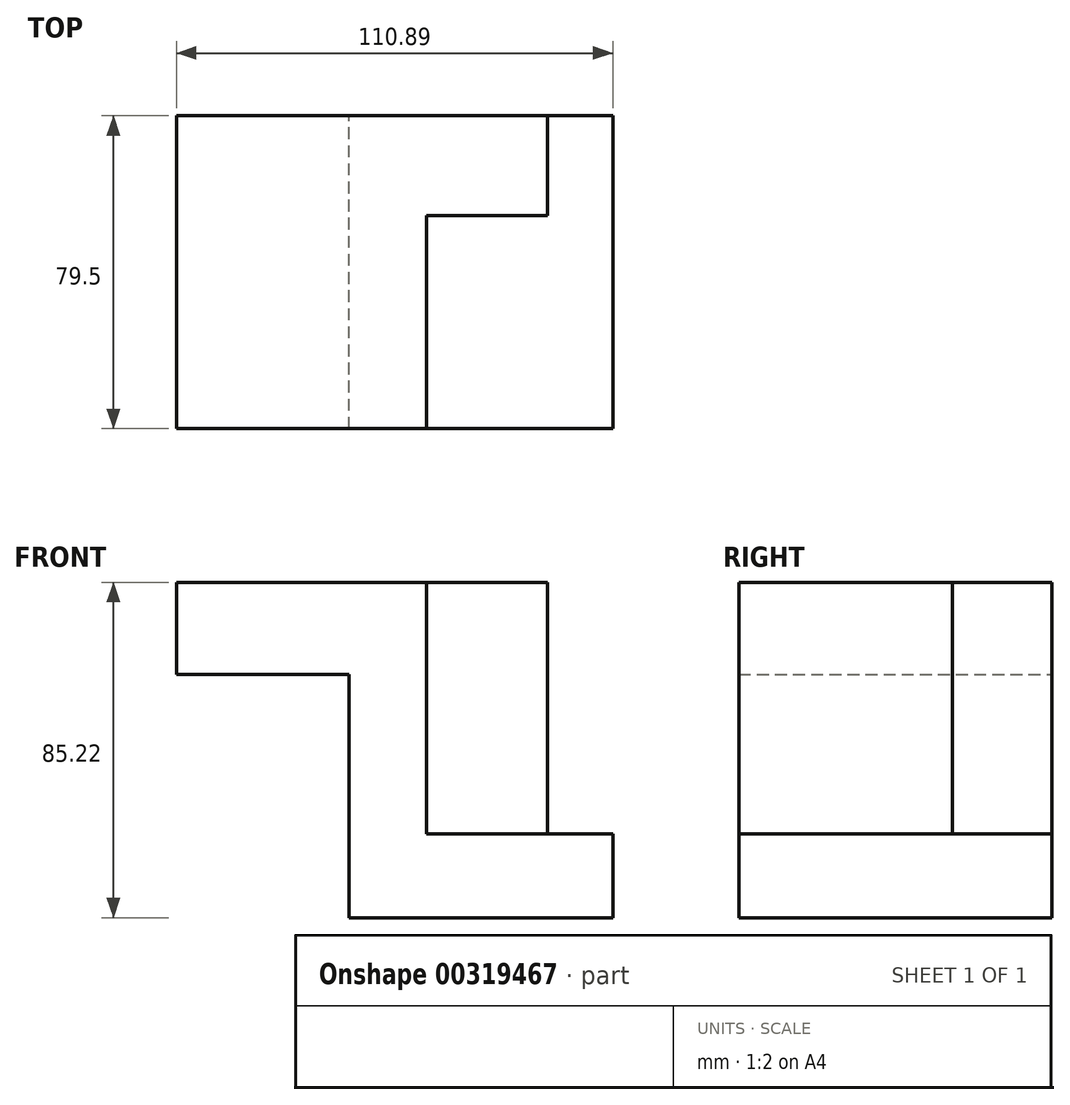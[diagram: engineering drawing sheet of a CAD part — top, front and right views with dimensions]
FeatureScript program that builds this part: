
annotation { "Feature Type Name" : "Feature", "Feature Type Description" : "" }
export const myFeature = defineFeature(function(context is Context, id is Id, definition is map)
    precondition{}
    {
        {
            var Q0;
            Q0=qCreatedBy(makeId("Front.planeOp"),FACE);
            var sketch = newSketch(context, id + "F0", { "sketchPlane" : qUnion([Q0])});
            skLineSegment(sketch, "E0", {"start": v(-68.88, 50.03) * mm, "end": v(-68.88, 26.57) * mm});
            skLineSegment(sketch, "E1", {"start": v(-68.88, 26.57) * mm, "end": v(-24.97, 26.57) * mm});
            skLineSegment(sketch, "E2", {"start": v(-24.97, 26.57) * mm, "end": v(-24.97, -35.2) * mm});
            skLineSegment(sketch, "E3", {"start": v(-24.97, -35.2) * mm, "end": v(42.01, -35.2) * mm});
            skLineSegment(sketch, "E4", {"start": v(42.01, -35.2) * mm, "end": v(42.01, -13.94) * mm});
            skLineSegment(sketch, "E5", {"start": v(42.01, -13.94) * mm, "end": v(-5.31, -13.94) * mm});
            skLineSegment(sketch, "E6", {"start": v(-5.31, -13.94) * mm, "end": v(-5.31, 50.03) * mm});
            skLineSegment(sketch, "E7", {"start": v(-5.31, 50.03) * mm, "end": v(-68.88, 50.03) * mm});
            skSolve(sketch);
        }
        {
            var Q0;
            Q0=makeQuery(id+"F0.imprint","IMPRINT",FACE,{"disambiguationData":[TD([[makeQuery(id+"F0.imprint","IMPRINT",EDGE,{"derivedFrom":sQuery(id+"F0.wireOp",EDGE,"E0")}),1.0]])]});
            extrude(context, id + "F1", {"entities" : qUnion([Q0]), "depth" : 79.5 * mm, "offsetDistance" : 25.4 * mm});
        }
        {
            var Q0;
            Q0=makeQuery(id+"F1.opExtrude","SWEPT_FACE",FACE,{"disambiguationData":[OSD([sQuery(id+"F0.wireOp",EDGE,"E6")])]});
            var sketch = newSketch(context, id + "F2", { "sketchPlane" : qUnion([Q0])});
            skLineSegment(sketch, "E8.bottom", {"start": v(0, -13.94) * mm, "end": v(-25.28, -13.94) * mm});
            skLineSegment(sketch, "E8.top", {"start": v(0, 50.03) * mm, "end": v(-25.28, 50.03) * mm});
            skLineSegment(sketch, "E8.left", {"start": v(0, -13.94) * mm, "end": v(0, 50.03) * mm});
            skLineSegment(sketch, "E8.right", {"start": v(-25.28, -13.94) * mm, "end": v(-25.28, 50.03) * mm});
            skSolve(sketch);
        }
        {
            var Q0;
            Q0 = qSketchRegion(id + "F2", true);
            extrude(context, id + "F3", {"entities" : qUnion([Q0]), "operationType" : NewBodyOperationType.ADD, "depth" : 30.73 * mm, "offsetDistance" : 25.4 * mm});
        }
    });
